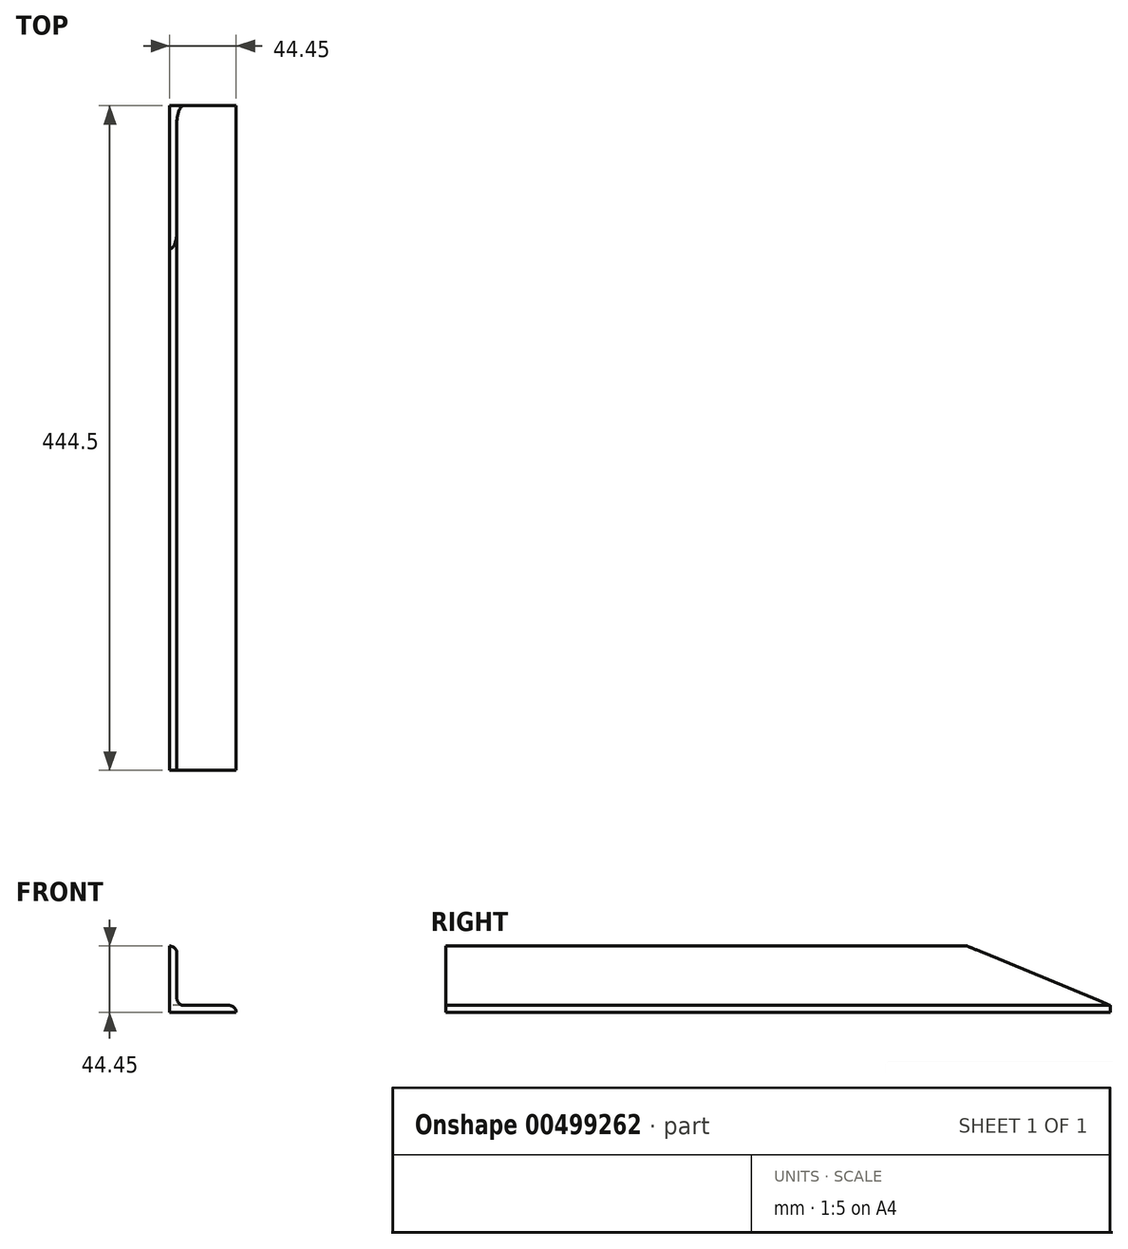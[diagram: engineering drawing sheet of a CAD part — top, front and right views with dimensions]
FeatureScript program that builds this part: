
annotation { "Feature Type Name" : "Feature", "Feature Type Description" : "" }
export const myFeature = defineFeature(function(context is Context, id is Id, definition is map)
    precondition{}
    {
        {
            var Q0;
            Q0=qCreatedBy(makeId("Front.planeOp"),FACE);
            var sketch = newSketch(context, id + "F0", { "sketchPlane" : qUnion([Q0])});
            skLineSegment(sketch, "E0", {"start": v(0, 0) * mm, "end": v(0, 44.45) * mm});
            skLineSegment(sketch, "E1", {"start": v(0, 0) * mm, "end": v(44.45, 0) * mm});
            skLineSegment(sketch, "E2.0", {"start": v(4.76, 0) * mm, "end": v(4.76, 44.45) * mm});
            skLineSegment(sketch, "E3.0", {"start": v(0, 4.76) * mm, "end": v(44.45, 4.76) * mm});
            skLineSegment(sketch, "E4", {"start": v(0, 44.45) * mm, "end": v(4.76, 44.45) * mm});
            skLineSegment(sketch, "E5", {"start": v(44.45, 4.76) * mm, "end": v(44.45, 0) * mm});
            skSolve(sketch);
        }
        {
            var Q0;
            Q0 = qSketchRegion(id + "F0", true);
            extrude(context, id + "F1", {"entities" : qUnion([Q0]), "endBound" : BoundingType.SYMMETRIC, "depth" : 444.5 * mm, "offsetDistance" : 25.4 * mm});
        }
        {
            var Q0;
            Q0=makeQuery(id+"F1.opExtrude","SWEPT_EDGE",EDGE,{"disambiguationData":[OSD([sQuery(id+"F0.wireOp",EDGE,"E2.0"),sQuery(id+"F0.wireOp",EDGE,"E3.0")])]});
            var Q1;
            Q1=makeQuery(id+"F1.opExtrude","SWEPT_EDGE",EDGE,{"disambiguationData":[OSD([sQuery(id+"F0.wireOp",EDGE,"E2.0"),sQuery(id+"F0.wireOp",EDGE,"E4")])]});
            var Q2;
            Q2=makeQuery(id+"F1.opExtrude","SWEPT_EDGE",EDGE,{"disambiguationData":[OSD([sQuery(id+"F0.wireOp",EDGE,"E3.0"),sQuery(id+"F0.wireOp",EDGE,"E5")])]});
            fillet(context, id + "F2", {"entities" : qUnion([Q0, Q1, Q2]), "radius" : 4.76 * mm, "tangentPropagation" : true, "allowEdgeOverflow" : false});
        }
        {
            var Q0;
            Q0=makeQuery(id+"F1.opExtrude","SWEPT_FACE",FACE,{"disambiguationData":[OSD([sQuery(id+"F0.wireOp",EDGE,"E0")])]});
            var sketch = newSketch(context, id + "F3", { "sketchPlane" : qUnion([Q0])});
            skPoint(sketch, "E6.0", {"position": v(-222.25, 4.76) * mm});
            skLineSegment(sketch, "E7", {"start": v(-222.25, 4.76) * mm, "end": v(-116.46, 48.58) * mm});
            skLineSegment(sketch, "E8", {"start": v(-222.25, 4.76) * mm, "end": v(-222.25, 44.45) * mm});
            skLineSegment(sketch, "E9", {"start": v(-222.25, 4.76) * mm, "end": v(-124.28, 4.76) * mm});
            skSolve(sketch);
        }
        {
            var Q0;
            Q0 = qSketchRegion(id + "F3", true);
            var Q1;
            {var subQ0=sQuery(id+"F3.wireOp",EDGE,"E8");Q1=makeQuery(id+"F3.imprint","IMPRINT",FACE,{"disambiguationData":[TD([[makeQuery(id+"F3.imprint","IMPRINT",EDGE,{"derivedFrom":subQ0}),-1.0]])]});}
            extrude(context, id + "F4", {"entities" : qUnion([Q0, Q1]), "operationType" : NewBodyOperationType.REMOVE, "oppositeDirection" : true, "depth" : 25.4 * mm});
        }
    });
